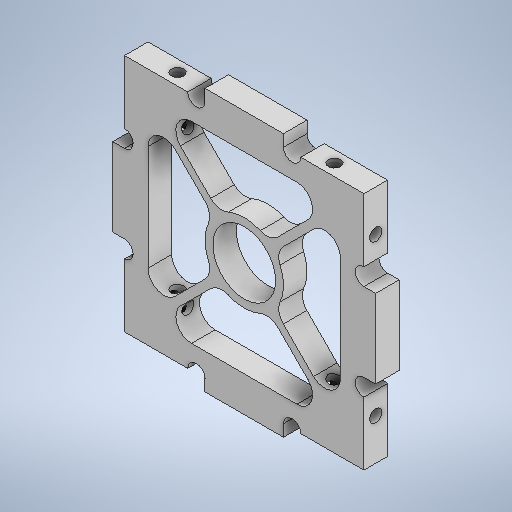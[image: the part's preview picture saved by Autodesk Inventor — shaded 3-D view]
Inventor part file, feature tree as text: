
AUTODESK INVENTOR PART (.ipt)
format: ipt  version: 2025.1 (Build 291241000, 241)  size: 399,872 bytes
history: native  units: mm
features: sketch x4, other x2, extrude x2, hole x2, fillet x1
ambient origin geometry x8: Origin, YZ Plane, XZ Plane, XY Plane, X Axis, Y Axis, Z Axis, Center Point
bodies: Body1 (feature_tree)
feature tree (11):
  other  "ソリッド1"
  extrude  "押し出し1"  Depth=30.5mm
  extrude  "押し出し2"  Depth=1.5mm
  fillet  "フィレット1"  Radius=10.0mm
  hole  "穴1"  [1 undecoded]
  hole  "穴2"  [1 undecoded]
  sketch  "スケッチ1"
  other  "スケッチ円形状パターン1"
  sketch  "スケッチ2"
  sketch  "スケッチ3"
  sketch  "スケッチ4"
note: 2 required parameter values undecoded (feature->parameter linkage not recoverable at this tier; creation-order binding heuristic only, values carry confidence <= 0.55)
